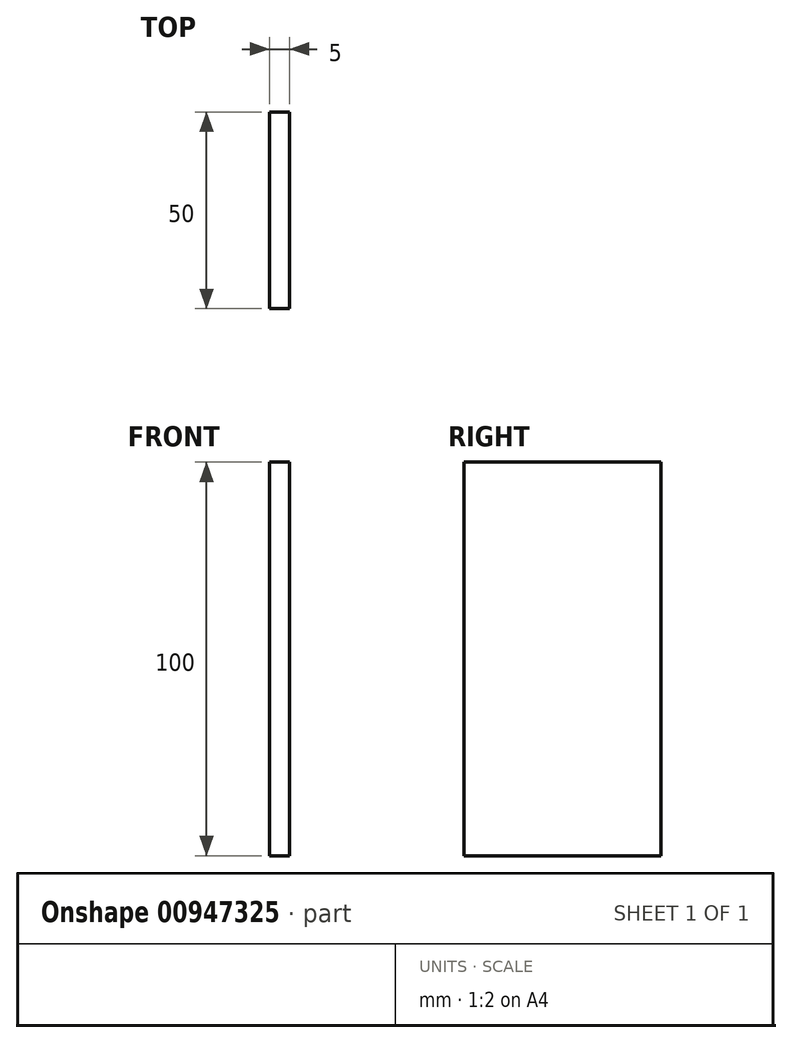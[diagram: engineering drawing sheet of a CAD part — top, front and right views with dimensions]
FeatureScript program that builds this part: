
annotation { "Feature Type Name" : "Feature", "Feature Type Description" : "" }
export const myFeature = defineFeature(function(context is Context, id is Id, definition is map)
    precondition{}
    {
        {
            var Q0;
            Q0=qCreatedBy(makeId("Right.planeOp"),FACE);
            var sketch = newSketch(context, id + "F0", { "sketchPlane" : qUnion([Q0])});
            skLineSegment(sketch, "E0.bottom", {"start": v(0, 0) * mm, "end": v(50, 0) * mm});
            skLineSegment(sketch, "E0.top", {"start": v(0, 100) * mm, "end": v(50, 100) * mm});
            skLineSegment(sketch, "E0.left", {"start": v(0, 0) * mm, "end": v(0, 100) * mm});
            skLineSegment(sketch, "E0.right", {"start": v(50, 0) * mm, "end": v(50, 100) * mm});
            skSolve(sketch);
        }
        {
            var Q0;
            Q0=makeQuery(id+"F0.imprint","IMPRINT",FACE,{"disambiguationData":[TD([[makeQuery(id+"F0.imprint","IMPRINT",EDGE,{"derivedFrom":sQuery(id+"F0.wireOp",EDGE,"E0.bottom")}),1.0]])]});
            extrude(context, id + "F1", {"entities" : qUnion([Q0]), "depth" : 5 * mm, "offsetDistance" : 25 * mm});
        }
    });
